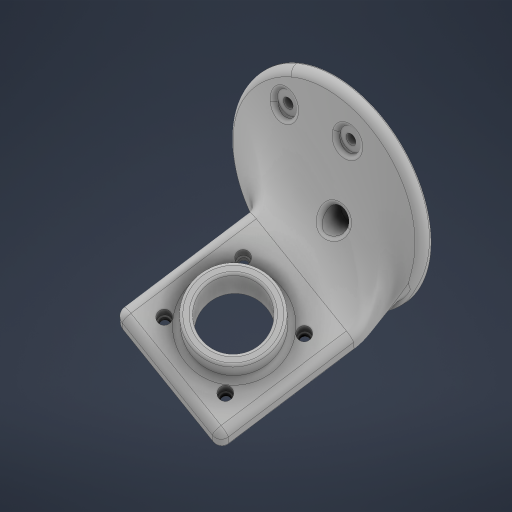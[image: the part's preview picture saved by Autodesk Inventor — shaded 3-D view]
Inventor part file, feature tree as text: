
AUTODESK INVENTOR PART (.ipt)
format: ipt  version: 2023 (Build 270158000, 158)  size: 733,696 bytes
history: native  units: in
note: dims shown in document units (in); Inventor stores cm internally (conversion verified against a paired STEP export)
features: extrude x1, sketch x1, other x1
ambient origin geometry x8: Origin, YZ Plane, XZ Plane, XY Plane, X Axis, Y Axis, Z Axis, Center Point
bodies: Solid1 (feature_tree)
feature tree (3):
  extrude  "Extrusion1"  [1 undecoded]
  sketch  "Sketch1"  dims[d0=0.3937in d1=0.0in]
  other  "6328-24b-1011 Right Wide Angle Camera Mount"
note: 1 required parameter value undecoded (feature->parameter linkage not recoverable at this tier; creation-order binding heuristic only, values carry confidence <= 0.55)
